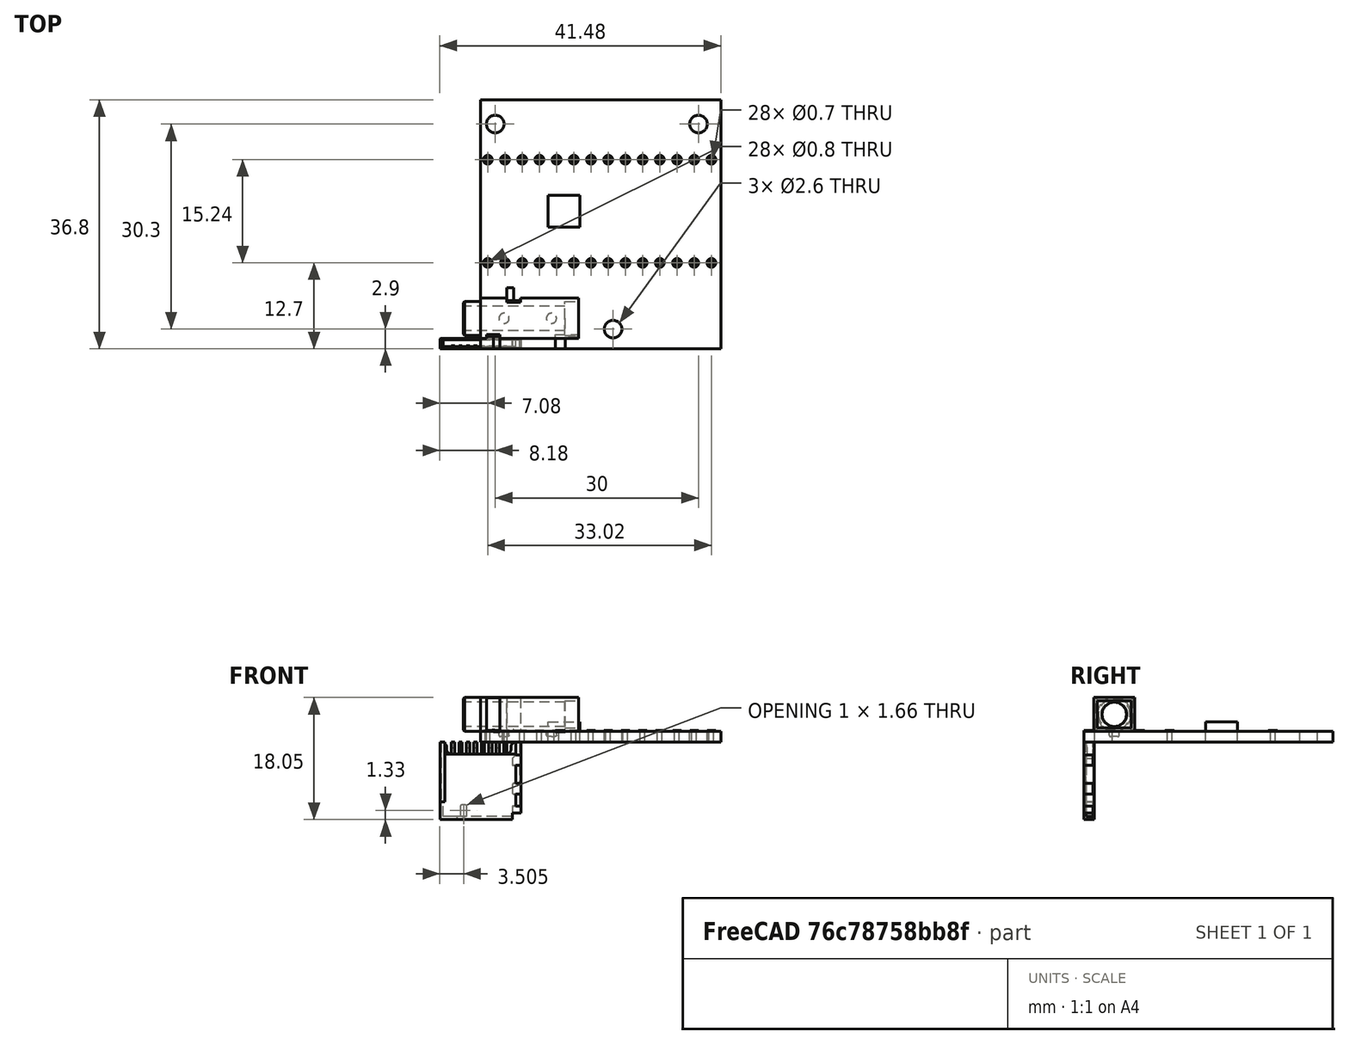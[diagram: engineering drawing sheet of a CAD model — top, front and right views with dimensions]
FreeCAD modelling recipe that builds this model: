
FCSTD DOCUMENT  (FreeCAD 0.18R16146 (Git))
Label: TeensyAudioBoard
License: All rights reserved
LicenseURL: http://en.wikipedia.org/wiki/All_rights_reserved
objects: Part::Cylinder×19, Part::Cut×19, Part::Feature×11, PartDesign::Body×8, Part::Compound×4, Part::Box×2, App::Part×2, Sketcher::SketchObject×1
note: 64 computed .brp shape members not serialized (recipe doc carries the construction recipe); baked Part::Feature solids carry a one-line shape summary decoded from their .brp

FEATURE [Part::Feature] Part__Feature  label="CUI_DEVICES_SJ-3523-SMT-TR"
  Placement = pos=(0,4.5,1.6) rot=(1,0,0;1.5708rad)
  shape: bbox 17 x 9 x 5.8 mm, 69 faces (baked)
FEATURE [Part::Box] Box  label="Cube"
  AttacherType = Attacher::AttachEngine3D
  Height = 1.6
  Length = 35.5
  Width = 36.8
FEATURE [Part::Cylinder] Cylinder
  Angle = 360
  AttacherType = Attacher::AttachEngine3D
  Height = 1.6
  Placement = pos=(19.6,2.9,0) rot=(0,0,1;0rad)
  Radius = 1.3
FEATURE [Part::Cut] Cut
  Base = -> Box
  Tool = -> Cylinder
FEATURE [Part::Cylinder] Cylinder001
  Angle = 360
  AttacherType = Attacher::AttachEngine3D
  Height = 1.6
  Placement = pos=(2.2,33.2,0) rot=(0,0,1;0rad)
  Radius = 1.3
FEATURE [Part::Cut] Cut001
  Base = -> Cut
  Tool = -> Cylinder001
FEATURE [Part::Cylinder] Cylinder002
  Angle = 360
  AttacherType = Attacher::AttachEngine3D
  Height = 1.6
  Placement = pos=(32.2,33.2,0) rot=(0,0,1;0rad)
  Radius = 1.3
FEATURE [Part::Cut] Cut002
  Base = -> Cut001
  Tool = -> Cylinder002
FEATURE [Part::Feature] Part__Feature043  label="Component047"
  shape: bbox 0.5 x 0.45 x 1.8 mm, 8 faces (baked)
FEATURE [Part::Feature] Part__Feature044  label="Component048"
  Placement = pos=(4.4,0,9e-15) rot=(0,0,1;0rad)
  shape: bbox 0.5 x 0.45 x 1.8 mm, 8 faces (baked)
FEATURE [Part::Feature] Part__Feature046  label="Component050"
  Placement = pos=(5.5,0,9e-15) rot=(0,0,1;0rad)
  shape: bbox 0.5 x 0.45 x 1.8 mm, 8 faces (baked)
FEATURE [Part::Feature] Part__Feature045  label="Component049"
  Placement = pos=(1.1,0,0) rot=(0,0,1;0rad)
  shape: bbox 0.5 x 0.45 x 1.8 mm, 8 faces (baked)
FEATURE [Part::Feature] Part__Feature047  label="Component051"
  Placement = pos=(6.6,0,0) rot=(0,0,1;0rad)
  shape: bbox 0.5 x 0.45 x 1.8 mm, 8 faces (baked)
FEATURE [Part::Feature] Part__Feature048  label="Component052"
  Placement = pos=(3.3,0,0) rot=(0,0,1;0rad)
  shape: bbox 0.5 x 0.45 x 1.8 mm, 8 faces (baked)
FEATURE [Part::Feature] Part__Feature049  label="Component053"
  Placement = pos=(2.2,0,0) rot=(0,0,1;0rad)
  shape: bbox 0.5 x 0.45 x 1.8 mm, 8 faces (baked)
FEATURE [Part::Feature] Part__Feature050  label="Case"
  shape: bbox 11.95 x 1.55 x 11.45 mm, 59 faces (baked)
FEATURE [Part::Feature] Part__Feature041  label="Base"
  shape: bbox 11.95 x 1.35 x 9.65 mm, 32 faces (baked)
FEATURE [Part::Feature] Part__Feature042  label="Component2"
  Placement = pos=(7.7,0,0) rot=(0,0,1;0rad)
  shape: bbox 0.5 x 0.45 x 1.8 mm, 8 faces (baked)
FEATURE [App::Part] Pins
  Group = -> [Part__Feature042,Part__Feature043,Part__Feature044,Part__Feature045,Part__Feature046,Part__Feature047,Part__Feature048,Part__Feature049]
  Origin = -> Origin006
FEATURE [PartDesign::Body] Body
  Origin = -> Origin
FEATURE [PartDesign::Body] Body001
  Origin = -> Origin008
FEATURE [PartDesign::Body] Body002
  Origin = -> Origin009
FEATURE [PartDesign::Body] Body003
  Origin = -> Origin010
FEATURE [PartDesign::Body] Body004
  Origin = -> Origin011
FEATURE [PartDesign::Body] Body005
  Origin = -> Origin012
FEATURE [PartDesign::Body] Body006
  Origin = -> Origin013
FEATURE [Sketcher::SketchObject] Sketch
  MapMode = 5
  Support = -> [XY_Plane014]
FEATURE [PartDesign::Body] Body007
  Group = -> [Sketch]
  Origin = -> Origin014
FEATURE [App::Part] HR5_DM3D_Micro_SD_Card_v4  label="HR5 DM3D Micro SD Card v4"
  Group = -> [Part__Feature041,Pins,Part__Feature050,Body,Body001,Body002,Body003,Body004,Body005,Body006,Body007]
  Origin = -> Origin007
  Placement = pos=(35.5,20.5,1.6) rot=(0.57735,0.57735,0.57735;2.0944rad)
FEATURE [Part::Cylinder] Cylinder004
  Angle = 360
  AttacherType = Attacher::AttachEngine3D
  Height = 1.6
  Placement = pos=(3.64,12.7,0) rot=(0,0,1;0rad)
  Radius = 0.35
FEATURE [Part::Cylinder] Cylinder006
  Angle = 360
  AttacherType = Attacher::AttachEngine3D
  Height = 0.1
  Placement = pos=(0,0,1.62) rot=(0,0,1;0rad)
  Radius = 0.65
FEATURE [Part::Cylinder] Cylinder007
  Angle = 360
  AttacherType = Attacher::AttachEngine3D
  Height = 0.1
  Placement = pos=(0,0,1.62) rot=(0,0,1;0rad)
  Radius = 0.4
FEATURE [Part::Cut] Cut003
  Base = -> Cylinder006
  Placement = pos=(1.1,12.7,0) rot=(0,0,1;0rad)
  Tool = -> Cylinder007
FEATURE [Part::Cylinder] Cylinder008
  Angle = 360
  AttacherType = Attacher::AttachEngine3D
  Height = 1.6
  Placement = pos=(1.1,12.7,0) rot=(0,0,1;0rad)
  Radius = 0.35
FEATURE [Part::Cylinder] Cylinder009
  Angle = 360
  AttacherType = Attacher::AttachEngine3D
  Height = 1.6
  Placement = pos=(8.72,12.7,0) rot=(0,0,1;0rad)
  Radius = 0.35
FEATURE [Part::Cylinder] Cylinder010
  Angle = 360
  AttacherType = Attacher::AttachEngine3D
  Height = 1.6
  Placement = pos=(6.18,12.7,0) rot=(0,0,1;0rad)
  Radius = 0.35
FEATURE [Part::Cylinder] Cylinder011
  Angle = 360
  AttacherType = Attacher::AttachEngine3D
  Height = 1.6
  Placement = pos=(11.26,12.7,0) rot=(0,0,1;0rad)
  Radius = 0.35
FEATURE [Part::Cylinder] Cylinder012
  Angle = 360
  AttacherType = Attacher::AttachEngine3D
  Height = 1.6
  Placement = pos=(13.8,12.7,0) rot=(0,0,1;0rad)
  Radius = 0.35
FEATURE [Part::Cylinder] Cylinder013
  Angle = 360
  AttacherType = Attacher::AttachEngine3D
  Height = 1.6
  Placement = pos=(18.88,12.7,0) rot=(0,0,1;0rad)
  Radius = 0.35
FEATURE [Part::Cylinder] Cylinder014
  Angle = 360
  AttacherType = Attacher::AttachEngine3D
  Height = 1.6
  Placement = pos=(23.96,12.7,0) rot=(0,0,1;0rad)
  Radius = 0.35
FEATURE [Part::Cylinder] Cylinder015
  Angle = 360
  AttacherType = Attacher::AttachEngine3D
  Height = 1.6
  Placement = pos=(21.42,12.7,0) rot=(0,0,1;0rad)
  Radius = 0.35
FEATURE [Part::Cylinder] Cylinder016
  Angle = 360
  AttacherType = Attacher::AttachEngine3D
  Height = 1.6
  Placement = pos=(16.34,12.7,0) rot=(0,0,1;0rad)
  Radius = 0.35
FEATURE [Part::Cylinder] Cylinder017
  Angle = 360
  AttacherType = Attacher::AttachEngine3D
  Height = 1.6
  Placement = pos=(29.04,12.7,0) rot=(0,0,1;0rad)
  Radius = 0.35
FEATURE [Part::Cylinder] Cylinder018
  Angle = 360
  AttacherType = Attacher::AttachEngine3D
  Height = 1.6
  Placement = pos=(34.12,12.7,0) rot=(0,0,1;0rad)
  Radius = 0.35
FEATURE [Part::Cylinder] Cylinder019
  Angle = 360
  AttacherType = Attacher::AttachEngine3D
  Height = 1.6
  Placement = pos=(31.58,12.7,0) rot=(0,0,1;0rad)
  Radius = 0.35
FEATURE [Part::Cylinder] Cylinder020
  Angle = 360
  AttacherType = Attacher::AttachEngine3D
  Height = 1.6
  Placement = pos=(26.5,12.7,0) rot=(0,0,1;0rad)
  Radius = 0.35
FEATURE [Part::Compound] Compound
  Links = -> [Cylinder004,Cylinder008,Cylinder009,Cylinder013,Cylinder018,Cylinder012,Cylinder015,Cylinder014,Cylinder016,Cylinder011,Cylinder010,Cylinder019,Cylinder020,Cylinder017]
FEATURE [Part::Compound] Compound001
  Links = -> [Cylinder004,Cylinder008,Cylinder009,Cylinder013,Cylinder018,Cylinder012,Cylinder015,Cylinder014,Cylinder016,Cylinder011,Cylinder010,Cylinder019,Cylinder020,Cylinder017]
  Placement = pos=(0,15.24,0) rot=(0,0,1;0rad)
FEATURE [Part::Cut] Cut004
  Base = -> Cut002
  Tool = -> Compound
FEATURE [Part::Cut] Cut005
  Base = -> Cut004
  Tool = -> Compound001
FEATURE [Part::Cut] Cut006
  Base = -> Cylinder006
  Placement = pos=(3.64,12.7,0) rot=(0,0,1;0rad)
  Tool = -> Cylinder007
FEATURE [Part::Cut] Cut008
  Base = -> Cylinder006
  Placement = pos=(8.72,12.7,0) rot=(0,0,1;0rad)
  Tool = -> Cylinder007
FEATURE [Part::Cut] Cut009
  Base = -> Cylinder006
  Placement = pos=(11.26,12.7,0) rot=(0,0,1;0rad)
  Tool = -> Cylinder007
FEATURE [Part::Cut] Cut010
  Base = -> Cylinder006
  Placement = pos=(13.8,12.7,0) rot=(0,0,1;0rad)
  Tool = -> Cylinder007
FEATURE [Part::Cut] Cut012
  Base = -> Cylinder006
  Placement = pos=(18.88,12.7,0) rot=(0,0,1;0rad)
  Tool = -> Cylinder007
FEATURE [Part::Cut] Cut013
  Base = -> Cylinder006
  Placement = pos=(21.42,12.7,0) rot=(0,0,1;0rad)
  Tool = -> Cylinder007
FEATURE [Part::Cut] Cut014
  Base = -> Cylinder006
  Placement = pos=(23.96,12.7,0) rot=(0,0,1;0rad)
  Tool = -> Cylinder007
FEATURE [Part::Cut] Cut015
  Base = -> Cylinder006
  Placement = pos=(26.5,12.7,0) rot=(0,0,1;0rad)
  Tool = -> Cylinder007
FEATURE [Part::Cut] Cut016
  Base = -> Cylinder006
  Placement = pos=(29.04,12.7,0) rot=(0,0,1;0rad)
  Tool = -> Cylinder007
FEATURE [Part::Cut] Cut017
  Base = -> Cylinder006
  Placement = pos=(31.58,12.7,0) rot=(0,0,1;0rad)
  Tool = -> Cylinder007
FEATURE [Part::Cut] Cut018
  Base = -> Cylinder006
  Placement = pos=(34.12,12.7,0) rot=(0,0,1;0rad)
  Tool = -> Cylinder007
FEATURE [Part::Cut] Cut011
  Base = -> Cylinder006
  Placement = pos=(16.34,12.7,0) rot=(0,0,1;0rad)
  Tool = -> Cylinder007
FEATURE [Part::Cut] Cut007
  Base = -> Cylinder006
  Placement = pos=(6.18,12.7,0) rot=(0,0,1;0rad)
  Tool = -> Cylinder007
FEATURE [Part::Compound] Compound002
  Links = -> [Cut003,Cut006,Cut018,Cut010,Cut016,Cut013,Cut011,Cut012,Cut017,Cut008,Cut015,Cut009,Cut014,Cut007]
FEATURE [Part::Compound] Compound003
  Links = -> [Cut003,Cut006,Cut018,Cut010,Cut016,Cut013,Cut011,Cut012,Cut017,Cut008,Cut015,Cut009,Cut014,Cut007]
  Placement = pos=(0,15.24,0) rot=(0,0,1;0rad)
FEATURE [Part::Box] Box001  label="Cube001"
  AttacherType = Attacher::AttachEngine3D
  Height = 3
  Length = 4.7
  Placement = pos=(10,18,0) rot=(0,0,1;0rad)
  Width = 4.7
